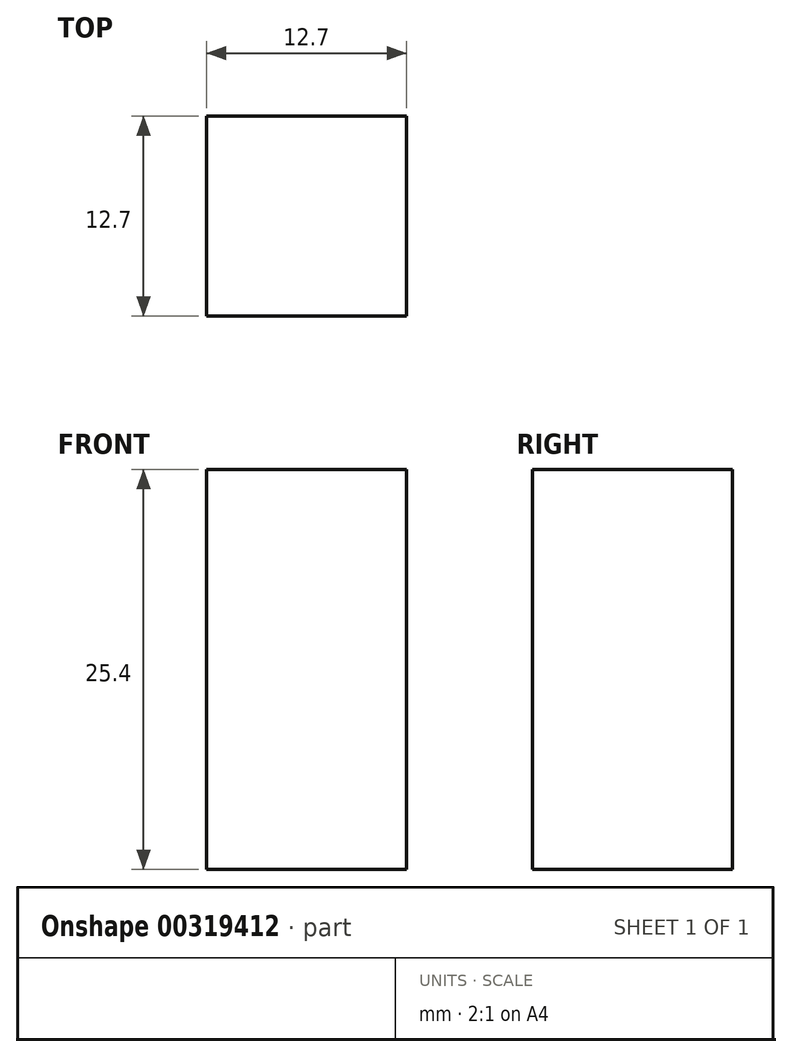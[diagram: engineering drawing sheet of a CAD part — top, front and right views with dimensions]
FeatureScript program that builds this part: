
annotation { "Feature Type Name" : "Feature", "Feature Type Description" : "" }
export const myFeature = defineFeature(function(context is Context, id is Id, definition is map)
    precondition{}
    {
        {
            var Q0;
            Q0=qCreatedBy(makeId("Top.planeOp"),FACE);
            var sketch = newSketch(context, id + "F0", { "sketchPlane" : qUnion([Q0])});
            skLineSegment(sketch, "E0.bottom", {"start": v(6.35, 6.35) * mm, "end": v(-6.35, 6.35) * mm});
            skLineSegment(sketch, "E0.top", {"start": v(6.35, -6.35) * mm, "end": v(-6.35, -6.35) * mm});
            skLineSegment(sketch, "E0.left", {"start": v(6.35, 6.35) * mm, "end": v(6.35, -6.35) * mm});
            skLineSegment(sketch, "E0.right", {"start": v(-6.35, 6.35) * mm, "end": v(-6.35, -6.35) * mm});
            skPoint(sketch, "E0.middle", {"position": v(0, 0) * mm});
            skSolve(sketch);
        }
        {
            var Q0;
            Q0=makeQuery(id+"F0.imprint","IMPRINT",FACE,{"disambiguationData":[TD([[makeQuery(id+"F0.imprint","IMPRINT",EDGE,{"derivedFrom":sQuery(id+"F0.wireOp",EDGE,"E0.bottom")}),1.0]])]});
            extrude(context, id + "F1", {"entities" : qUnion([Q0]), "depth" : 25.4 * mm, "offsetDistance" : 25.4 * mm});
        }
    });
